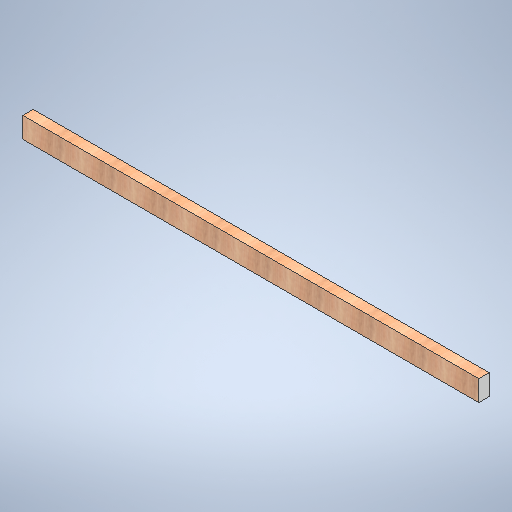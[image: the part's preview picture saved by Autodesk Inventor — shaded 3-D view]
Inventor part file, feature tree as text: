
AUTODESK INVENTOR PART (.ipt)
format: ipt  version: 2025 (Build 290162000, 162)  size: 299,520 bytes
history: native  units: in
note: dims shown in document units (in); Inventor stores cm internally (conversion verified against a paired STEP export)
features: extrude x2, sketch x2
ambient origin geometry x8: Origin, YZ Plane, XZ Plane, XY Plane, X Axis, Y Axis, Z Axis, Center Point
bodies: Solid1 (feature_tree)
feature tree (4):
  extrude  "Extrusion1"  Depth=4.0in
  extrude  "Extrusion2"  Depth=2.0in TaperAngle=0.0deg
  sketch  "Sketch1"  dims[d0=96.0in d1=4.0in]
  sketch  "Sketch2"  dims[d2=2.0in d3=0.0in d4=8.0in d5=0.0in]
